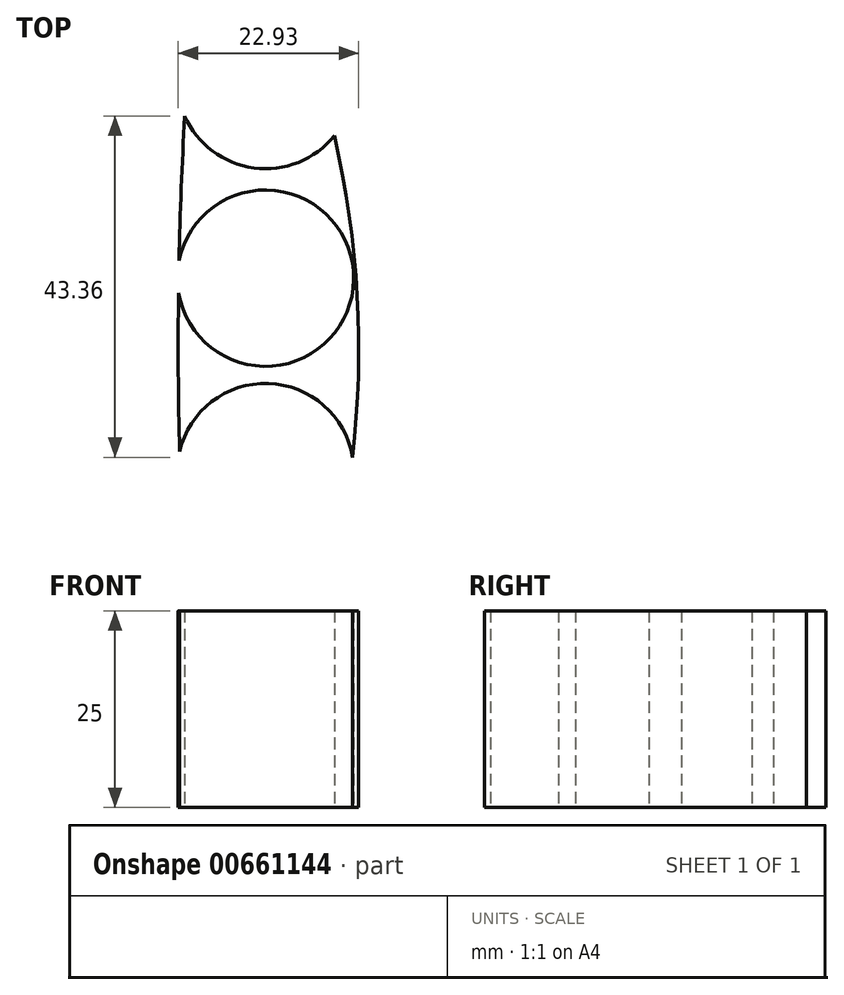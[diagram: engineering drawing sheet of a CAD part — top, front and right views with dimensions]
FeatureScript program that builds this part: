
annotation { "Feature Type Name" : "Feature", "Feature Type Description" : "" }
export const myFeature = defineFeature(function(context is Context, id is Id, definition is map)
    precondition{}
    {
        {
            var Q0;
            Q0=qCreatedBy(makeId("Top.planeOp"),FACE);
            var sketch = newSketch(context, id + "F0", { "sketchPlane" : qUnion([Q0])});
            skCircle(sketch, "E0", {"center": v(0, 0) * mm, "radius": 11.2 * mm});
            skCircle(sketch, "E1", {"center": v(0, -24.57) * mm, "radius": 11.2 * mm});
            skCircle(sketch, "E2", {"center": v(0, 25.1) * mm, "radius": 11.2 * mm});
            skArc(sketch, "E3", {"start": v(-10.26, 20.61) * mm, "mid": v(-11.03, -0.7) * mm, "end": v(-10.91, -22.04) * mm});
            skArc(sketch, "E4", {"start": v(11.05, -22.75) * mm, "mid": v(11.64, -2.23) * mm, "end": v(8.74, 18.1) * mm});
            skSolve(sketch);
        }
        {
            var Q0;
            {var subQ3=sQuery(id+"F0.wireOp",EDGE,"E4");Q0=makeQuery(id+"F0.imprint","IMPRINT",FACE,{"disambiguationData":[TD([[makeQuery(id+"F0.imprint","IMPRINT",EDGE,{"derivedFrom":subQ3}),1.0]])]});}
            extrude(context, id + "F1", {"entities" : qUnion([Q0]), "depth" : 25 * mm, "offsetDistance" : 25 * mm});
        }
    });
